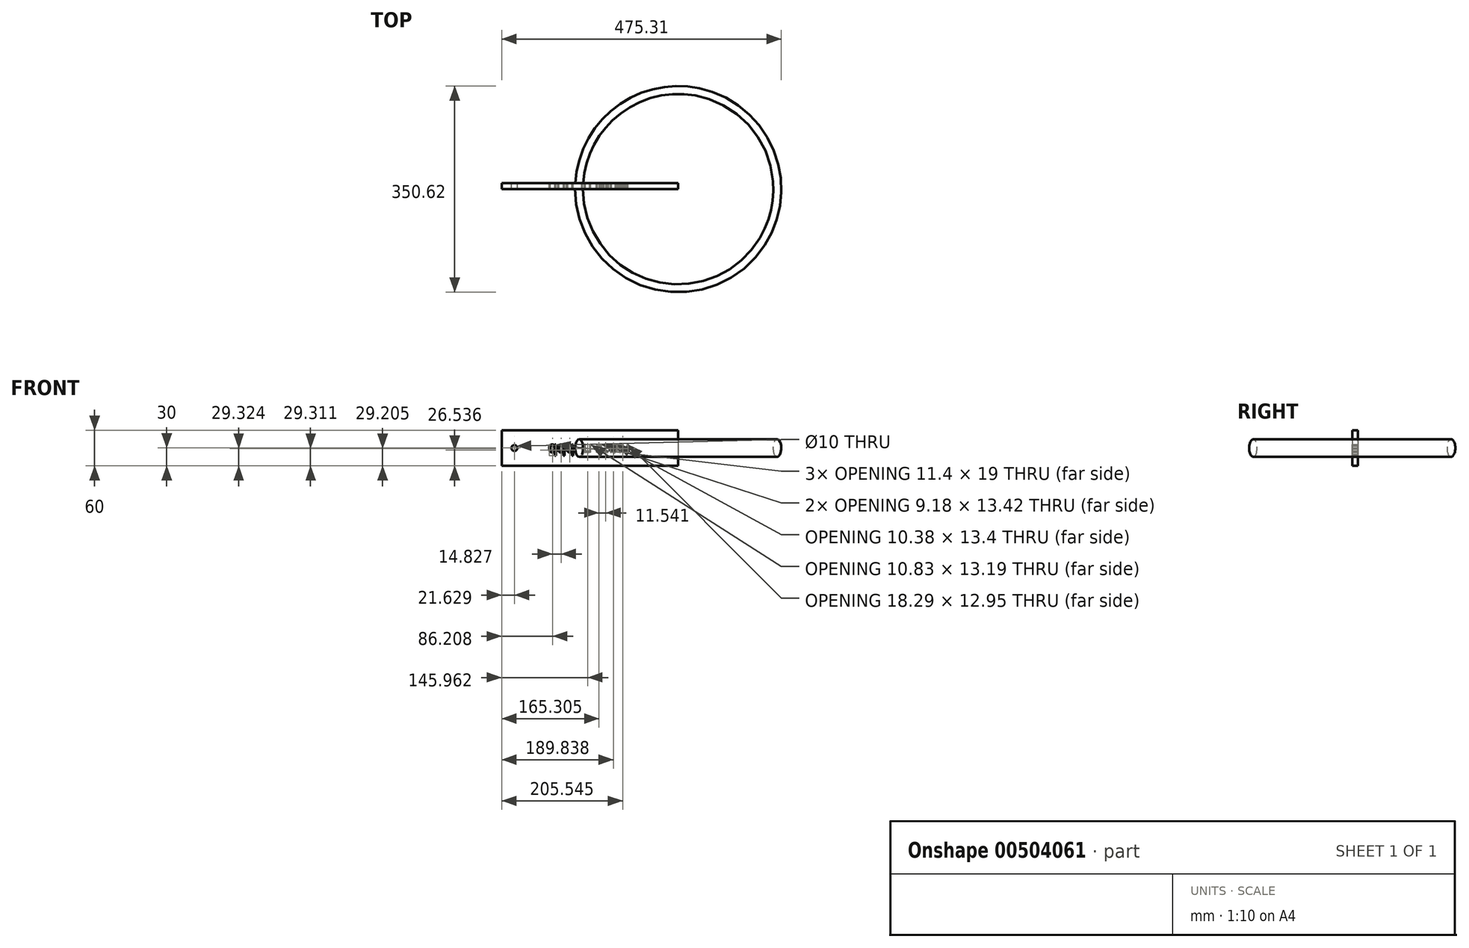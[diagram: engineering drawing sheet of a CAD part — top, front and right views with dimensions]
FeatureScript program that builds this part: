
annotation { "Feature Type Name" : "Feature", "Feature Type Description" : "" }
export const myFeature = defineFeature(function(context is Context, id is Id, definition is map)
    precondition{}
    {
        {
            var Q0;
            Q0=qCreatedBy(makeId("Front.planeOp"),FACE);
            var sketch = newSketch(context, id + "F0", { "sketchPlane" : qUnion([Q0])});
            skLineSegment(sketch, "E0.bottom", {"start": v(150, 30) * mm, "end": v(-150, 30) * mm});
            skLineSegment(sketch, "E0.top", {"start": v(150, -30) * mm, "end": v(-150, -30) * mm});
            skLineSegment(sketch, "E0.left", {"start": v(150, 30) * mm, "end": v(150, -30) * mm});
            skLineSegment(sketch, "E0.right", {"start": v(-150, 30) * mm, "end": v(-150, -30) * mm});
            skPoint(sketch, "E0.middle", {"position": v(0, 0) * mm});
            skSolve(sketch);
        }
        {
            var Q0;
            Q0=makeQuery(id+"F0.imprint","IMPRINT",FACE,{"disambiguationData":[TD([[makeQuery(id+"F0.imprint","IMPRINT",EDGE,{"derivedFrom":sQuery(id+"F0.wireOp",EDGE,"E0.bottom")}),1.0]])]});
            extrude(context, id + "F1", {"entities" : qUnion([Q0]), "oppositeDirection" : true, "depth" : 10 * mm});
        }
        {
            var Q0;
            Q0=makeQuery(id+"F1.opExtrude","CAP_FACE",FACE,{"disambiguationData":[OSD([sQuery(id+"F0.wireOp",EDGE,"E0.bottom"),sQuery(id+"F0.wireOp",EDGE,"E0.top"),sQuery(id+"F0.wireOp",EDGE,"E0.left"),sQuery(id+"F0.wireOp",EDGE,"E0.right")])],"isStart":false});
            var sketch = newSketch(context, id + "F2", { "sketchPlane" : qUnion([Q0])});
            skText(sketch, "E1", { "text": "wass upppp", "fontName": "OpenSans-Regular.ttf"});
            const initialGuessF2  = {"E1": [-0.06496, -0.00715, 1, 0, 0.01742]};
            skSetInitialGuess(sketch, initialGuessF2);
            skSolve(sketch);
        }
        {
            var Q0;
            Q0 = qSketchRegion(id + "F2", true);
            extrude(context, id + "F3", {"entities" : qUnion([Q0]), "operationType" : NewBodyOperationType.REMOVE, "oppositeDirection" : true, "depth" : 25 * mm});
        }
        {
            var Q0;
            Q0=qCreatedBy(makeId("Right.planeOp"),FACE);
            var sketch = newSketch(context, id + "F4", { "sketchPlane" : qUnion([Q0])});
            skCircle(sketch, "E2", {"center": v(-75.73, 0) * mm, "radius": 15 * mm});
            skSolve(sketch);
        }
        {
            var Q0;
            Q0=makeQuery(id+"F4.imprint","IMPRINT",FACE,{"disambiguationData":[TD([[makeQuery(id+"F4.imprint","IMPRINT",EDGE,{"derivedFrom":sQuery(id+"F4.wireOp",EDGE,"E2")}),1.0]])]});
            var Q1;
            Q1=makeQuery(id+"F1.opExtrude","CAP_EDGE",EDGE,{"disambiguationData":[OSD([sQuery(id+"F0.wireOp",EDGE,"E0.left")])],"isStart":true});
            revolve(context, id + "F5", {"operationType" : NewBodyOperationType.ADD, "entities" : qUnion([Q0]), "axis" : qUnion([Q1]), "revolveType" : RevolveType.FULL});
        }
        {
            var Q0;
            {var subQ0=sQuery(id+"F0.wireOp",EDGE,"E0.top");var subQ1=sQuery(id+"F0.wireOp",EDGE,"E0.right");var subQ2=sQuery(id+"F0.wireOp",EDGE,"E0.bottom");var subQ3=sQuery(id+"F0.wireOp",EDGE,"E0.left");Q0=makeQuery(id+"F3.boolean.opBoolean","SPLIT",FACE,{"disambiguationData":[TD([makeQuery(id+"F1.opExtrude","SWEPT_FACE",FACE,{"disambiguationData":[OSD([subQ2])]})])],"derivedFrom":makeQuery(id+"F1.opExtrude","CAP_FACE",FACE,{"disambiguationData":[OSD([subQ2,subQ0,subQ3,subQ1])],"isStart":false})});}
            var sketch = newSketch(context, id + "F6", { "sketchPlane" : qUnion([Q0])});
            skCircle(sketch, "E3", {"center": v(128.37, 0) * mm, "radius": 5 * mm});
            skSolve(sketch);
        }
        {
            var Q0;
            Q0=makeQuery(id+"F6.imprint","IMPRINT",FACE,{"disambiguationData":[TD([[makeQuery(id+"F6.imprint","IMPRINT",EDGE,{"derivedFrom":sQuery(id+"F6.wireOp",EDGE,"E3")}),1.0]])]});
            extrude(context, id + "F7", {"entities" : qUnion([Q0]), "operationType" : NewBodyOperationType.REMOVE, "oppositeDirection" : true, "depth" : 25 * mm});
        }
    });
